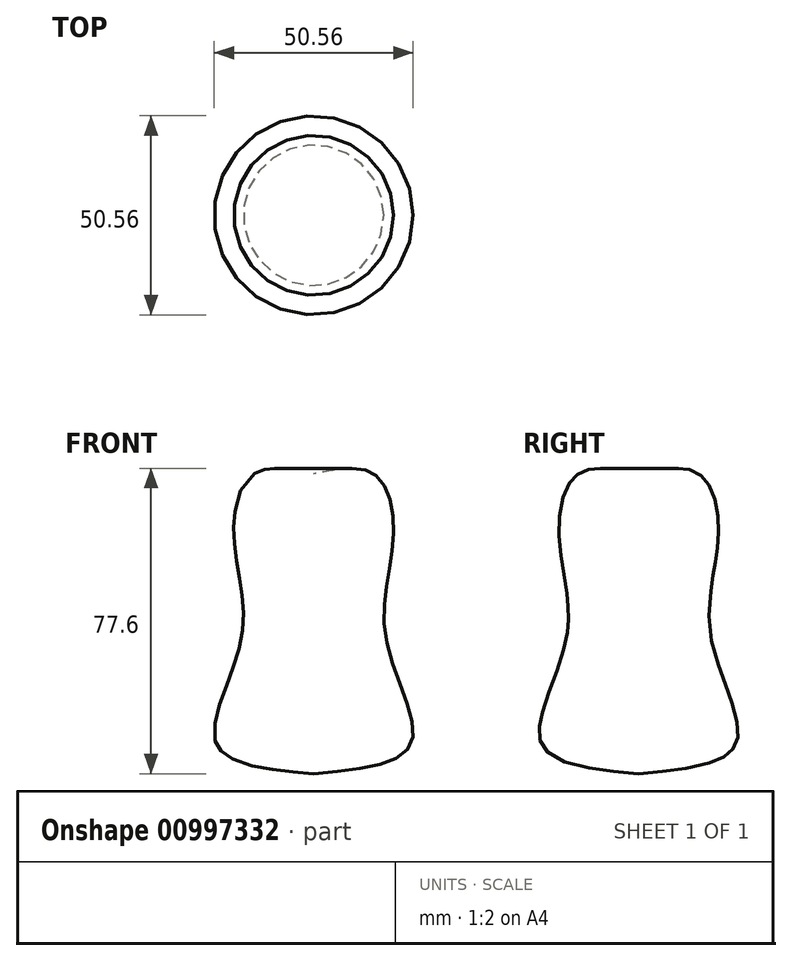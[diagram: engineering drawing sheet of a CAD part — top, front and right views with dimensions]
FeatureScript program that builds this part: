
annotation { "Feature Type Name" : "Feature", "Feature Type Description" : "" }
export const myFeature = defineFeature(function(context is Context, id is Id, definition is map)
    precondition{}
    {
        {
            var Q0;
            Q0=qCreatedBy(makeId("Front.planeOp"),FACE);
            var sketch = newSketch(context, id + "F0", { "sketchPlane" : qUnion([Q0])});
            skLineSegment(sketch, "E0", {"start": v(0, 0) * mm, "end": v(0, 76.12) * mm});
            skFitSpline(sketch, "E1", {"points": [v(0, 0) * mm, v(24.8, 7.77) * mm, v(18.36, 34.3) * mm, v(20.24, 59.77) * mm, v(15.41, 76.12) * mm, v(0, 76.12) * mm], "startDerivative": vector(155, 13.6) * mm, "endDerivative": vector(-105.28, -22.88) * mm});
            skSolve(sketch);
        }
        {
            var Q0;
            Q0=makeQuery(id+"F0.imprint","IMPRINT",FACE,{"disambiguationData":[TD([[makeQuery(id+"F0.imprint","IMPRINT",EDGE,{"derivedFrom":sQuery(id+"F0.wireOp",EDGE,"E0")}),-1.0]])]});
            var Q1;
            Q1=sQuery(id+"F0.wireOp",EDGE,"E0");
            revolve(context, id + "F1", {"surfaceOperationType" : NewSurfaceOperationType.NEW, "entities" : qUnion([Q0]), "axis" : qUnion([Q1]), "revolveType" : RevolveType.FULL});
        }
    });
